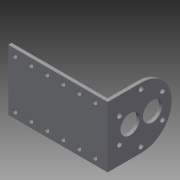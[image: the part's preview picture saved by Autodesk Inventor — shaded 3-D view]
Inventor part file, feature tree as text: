
AUTODESK INVENTOR PART (.ipt)
format: ipt  version: 2013 (Build 170138000, 138)  size: 155,136 bytes
history: native  units: mm
features: sketch x4, extrude x3, other x1, hole x1, fillet x1
ambient origin geometry x8: Origin, YZ Plane, XZ Plane, XY Plane, X Axis, Y Axis, Z Axis, Center Point
feature tree (10):
  other  "ソリッド1"
  extrude  "押し出し1"  Depth=62.0mm
  hole  "穴1"  [1 undecoded]
  extrude  "押し出し2"  Depth=2.0mm TaperAngle=0.0deg
  fillet  "フィレット1"  Radius=4.0mm
  extrude  "押し出し3"  Depth=4.0mm
  sketch  "スケッチ1"
  sketch  "スケッチ2"
  sketch  "スケッチ3"
  sketch  "スケッチ4"
note: 1 required parameter value undecoded (feature->parameter linkage not recoverable at this tier; creation-order binding heuristic only, values carry confidence <= 0.55)
